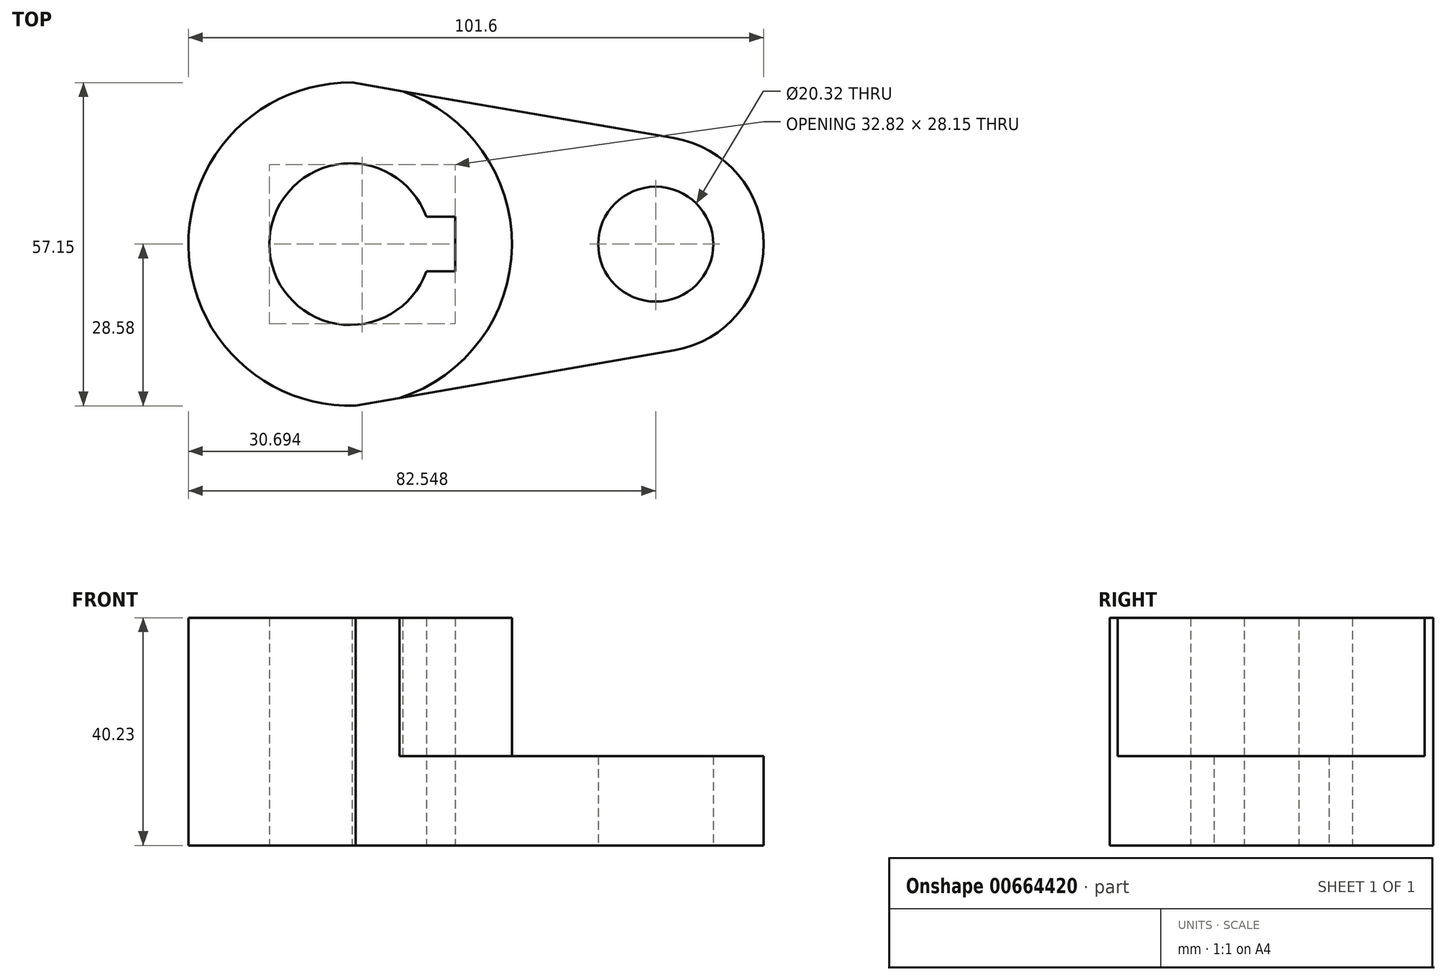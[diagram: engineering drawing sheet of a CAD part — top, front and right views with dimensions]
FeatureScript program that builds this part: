
annotation { "Feature Type Name" : "Feature", "Feature Type Description" : "" }
export const myFeature = defineFeature(function(context is Context, id is Id, definition is map)
    precondition{}
    {
        {
            var Q0;
            Q0=qCreatedBy(makeId("Top.planeOp"),FACE);
            var sketch = newSketch(context, id + "F0", { "sketchPlane" : qUnion([Q0])});
            skLineSegment(sketch, "E0", {"start": v(-24.64, 0) * mm, "end": v(29.34, 0) * mm});
            skCircle(sketch, "E1", {"center": v(-24.64, 0) * mm, "radius": 14.29 * mm});
            skCircle(sketch, "E2", {"center": v(29.34, 0) * mm, "radius": 10.16 * mm});
            skCircle(sketch, "E3", {"center": v(-24.64, 0) * mm, "radius": 28.58 * mm});
            skCircle(sketch, "E4", {"center": v(29.34, 0) * mm, "radius": 19.05 * mm});
            skLineSegment(sketch, "E5", {"start": v(-24.31, 28.57) * mm, "end": v(32.57, 18.77) * mm});
            skLineSegment(sketch, "E6", {"start": v(-23.67, -28.56) * mm, "end": v(32.6, -18.77) * mm});
            skLineSegment(sketch, "E7", {"start": v(-38.92, 0) * mm, "end": v(-6.1, 0) * mm});
            skLineSegment(sketch, "E8", {"start": v(-6.1, 0) * mm, "end": v(-6.1, 4.83) * mm});
            skLineSegment(sketch, "E9", {"start": v(-6.1, 4.83) * mm, "end": v(-6.1, -4.83) * mm});
            skLineSegment(sketch, "E10", {"start": v(-6.1, -4.83) * mm, "end": v(-11.19, -4.83) * mm});
            skLineSegment(sketch, "E11", {"start": v(-6.1, 4.83) * mm, "end": v(-11.19, 4.83) * mm});
            skSolve(sketch);
        }
        {
            var Q0;
            {var subQ0=sQuery(id+"F0.wireOp",EDGE,"E5");var subQ1=sQuery(id+"F0.wireOp",EDGE,"E3");var subQ2=makeQuery(id+"F0.imprint","INTERSECT",VERTEX,{"disambiguationData":[OD(0.0)],"derivedFrom":[subQ1,subQ0]});Q0=makeQuery(id+"F0.imprint","IMPRINT",FACE,{"disambiguationData":[TD([[makeQuery(id+"F0.imprint","IMPRINT",EDGE,{"disambiguationData":[TD([[subQ2,1.0]])],"derivedFrom":subQ1}),1.0]])]});}
            var Q1;
            {var subQ0=sQuery(id+"F0.wireOp",EDGE,"E6");var subQ1=sQuery(id+"F0.wireOp",EDGE,"E3");var subQ2=makeQuery(id+"F0.imprint","INTERSECT",VERTEX,{"disambiguationData":[OD(0.0)],"derivedFrom":[subQ1,subQ0]});Q1=makeQuery(id+"F0.imprint","IMPRINT",FACE,{"disambiguationData":[TD([[makeQuery(id+"F0.imprint","IMPRINT",EDGE,{"disambiguationData":[TD([[subQ2,-1.0]])],"derivedFrom":subQ1}),1.0]])]});}
            var Q2;
            Q2=makeQuery(id+"F0.imprint","IMPRINT",FACE,{"disambiguationData":[TD([[makeQuery(id+"F0.imprint","IMPRINT",EDGE,{"derivedFrom":sQuery(id+"F0.wireOp",EDGE,"E1")}),-1.0]])]});
            extrude(context, id + "F1", {"entities" : qUnion([Q0, Q1, Q2]), "depth" : 40.23 * mm, "offsetDistance" : 25.4 * mm});
        }
        {
            var Q0;
            {var subQ0=sQuery(id+"F0.wireOp",EDGE,"E3");var subQ1=sQuery(id+"F0.wireOp",EDGE,"E0");var subQ2=makeQuery(id+"F0.imprint","INTERSECT",VERTEX,{"derivedFrom":[subQ1,subQ0]});Q0=makeQuery(id+"F0.imprint","IMPRINT",FACE,{"disambiguationData":[TD([[makeQuery(id+"F0.imprint","IMPRINT",EDGE,{"disambiguationData":[TD([[subQ2,-1.0]])],"derivedFrom":subQ1}),-1.0]])]});}
            var Q1;
            {var subQ0=sQuery(id+"F0.wireOp",EDGE,"E3");var subQ1=sQuery(id+"F0.wireOp",EDGE,"E0");var subQ2=makeQuery(id+"F0.imprint","INTERSECT",VERTEX,{"derivedFrom":[subQ1,subQ0]});Q1=makeQuery(id+"F0.imprint","IMPRINT",FACE,{"disambiguationData":[TD([[makeQuery(id+"F0.imprint","IMPRINT",EDGE,{"disambiguationData":[TD([[subQ2,-1.0]])],"derivedFrom":subQ1}),1.0]])]});}
            var Q2;
            Q2=makeQuery(id+"F0.imprint","IMPRINT",FACE,{"disambiguationData":[TD([[makeQuery(id+"F0.imprint","IMPRINT",EDGE,{"derivedFrom":sQuery(id+"F0.wireOp",EDGE,"E2")}),-1.0]])]});
            extrude(context, id + "F2", {"entities" : qUnion([Q0, Q1, Q2]), "operationType" : NewBodyOperationType.ADD, "depth" : 15.77 * mm, "offsetDistance" : 25.4 * mm});
        }
    });
